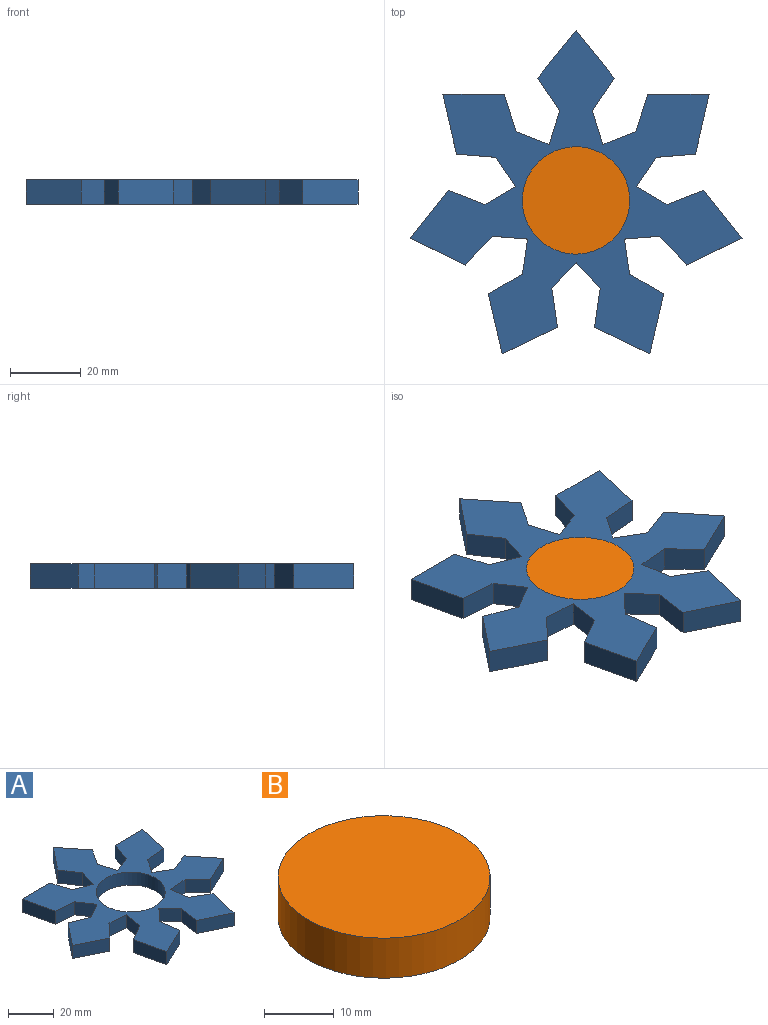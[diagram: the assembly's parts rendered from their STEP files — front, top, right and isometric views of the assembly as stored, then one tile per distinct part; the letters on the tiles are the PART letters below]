
ASSEMBLY  parts=2 mates=1
PART A: 45 faces, bbox 93.6x91.3x7 mm
  f0: plane 8.62x7mm, normal (0.5,0.86,0), area 69.9mm2, adj f1,f42,f43,f44
  f1: plane 8.27x7mm, normal (0.83,-0.56,0), area 69.9mm2, adj f0,f2,f43,f44
  f2: plane 11.07x7mm, normal (0.08,-1,0), area 77.7mm2, adj f1,f3,f43,f44
  f3: plane 16.89x7mm, normal (0.98,-0.22,0), area 121.2mm2, adj f2,f4,f43,f44
  f4: plane 17.32x7mm, normal (0,1,0), area 121.2mm2, adj f3,f5,f43,f44
  f5: plane 10.59x7mm, normal (-0.95,0.3,0), area 77.7mm2, adj f4,f6,f43,f44
  f6: plane 9.31x7mm, normal (-0.36,0.93,0), area 69.9mm2, adj f5,f7,f43,f44
  f7: plane 9.52x7mm, normal (0.95,0.3,0), area 69.9mm2, adj f6,f8,f43,f44
  f8: plane 9.21x7mm, normal (0.83,-0.56,0), area 77.7mm2, adj f7,f9,f43,f44
  f9: plane 13.53x10.81mm, normal (0.78,0.62,0), area 121.2mm2, adj f8,f10,f43,f44
  f10: plane 13.53x10.81mm, normal (-0.78,0.62,0), area 121.2mm2, adj f9,f11,f43,f44
  f11: plane 9.21x7mm, normal (-0.83,-0.56,0), area 77.7mm2, adj f10,f12,f43,f44
  f12: plane 9.52x7mm, normal (-0.95,0.3,0), area 69.9mm2, adj f11,f13,f43,f44
  f13: plane 9.31x7mm, normal (0.36,0.93,0), area 69.9mm2, adj f12,f14,f43,f44
  f14: plane 10.59x7mm, normal (0.95,0.3,0), area 77.7mm2, adj f13,f15,f43,f44
  f15: plane 17.32x7mm, normal (0,1,0), area 121.2mm2, adj f14,f16,f43,f44
  f16: plane 16.89x7mm, normal (-0.98,-0.22,0), area 121.2mm2, adj f15,f17,f43,f44
  f17: plane 11.07x7mm, normal (-0.08,-1,0), area 77.7mm2, adj f16,f18,f43,f44
  f18: plane 8.27x7mm, normal (-0.83,-0.56,0), area 69.9mm2, adj f17,f19,f43,f44
  f19: plane 8.62x7mm, normal (-0.5,0.86,0), area 69.9mm2, adj f18,f20,f43,f44
  f20: plane 10.36x7mm, normal (0.36,0.93,0), area 77.7mm2, adj f19,f21,f43,f44
  f21: plane 13.55x10.79mm, normal (-0.78,0.62,0), area 121.2mm2, adj f20,f22,f43,f44
  f22: plane 15.6x7.53mm, normal (-0.43,-0.9,0), area 121.2mm2, adj f21,f23,f43,f44
  f23: plane 8.1x7.6mm, normal (0.73,-0.68,0), area 77.7mm2, adj f22,f24,f43,f44
  f24: plane 9.95x7mm, normal (-0.08,-1,0), area 69.9mm2, adj f23,f25,f43,f44
  f25: plane 9.88x7mm, normal (-0.99,0.14,0), area 69.9mm2, adj f24,f26,f43,f44
  f26: plane 9.58x7mm, normal (-0.5,0.86,0), area 77.7mm2, adj f25,f27,f43,f44
  f27: plane 16.88x7mm, normal (-0.97,-0.22,0), area 121.2mm2, adj f26,f28,f43,f44
  f28: plane 15.61x7.5mm, normal (0.43,-0.9,0), area 121.2mm2, adj f27,f29,f43,f44
  f29: plane 10.99x7mm, normal (0.99,0.14,0), area 77.7mm2, adj f28,f30,f43,f44
  f30: plane 7.29x7mm, normal (0.73,-0.68,0), area 69.9mm2, adj f29,f31,f43,f44
  f31: plane 7.29x7mm, normal (-0.73,-0.68,0), area 69.9mm2, adj f30,f32,f43,f44
  f32: plane 10.99x7mm, normal (-0.99,0.14,0), area 77.7mm2, adj f31,f33,f43,f44
  f33: plane 15.61x7.5mm, normal (-0.43,-0.9,0), area 121.2mm2, adj f32,f34,f43,f44
  f34: plane 16.88x7mm, normal (0.97,-0.22,0), area 121.2mm2, adj f33,f35,f43,f44
  f35: plane 9.58x7mm, normal (0.5,0.86,0), area 77.7mm2, adj f34,f36,f43,f44
  f36: plane 9.88x7mm, normal (0.99,0.14,0), area 69.9mm2, adj f35,f37,f43,f44
  f37: plane 9.95x7mm, normal (0.08,-1,0), area 69.9mm2, adj f36,f38,f43,f44
  f38: plane 8.1x7.6mm, normal (-0.73,-0.68,0), area 77.7mm2, adj f37,f39,f43,f44
  f39: plane 15.6x7.53mm, normal (0.43,-0.9,0), area 121.2mm2, adj f38,f40,f43,f44
  f40: plane 13.55x10.79mm, normal (0.78,0.62,0), area 121.2mm2, adj f39,f42,f43,f44
  f41: cylinder r=15.16mm len=30.31mm, axis (0,0,-1), area 666.6mm2, adj f43,f44
  f42: plane 10.36x7mm, normal (-0.36,0.93,0), area 77.7mm2, adj f0,f40,f43,f44
  f43: plane 93.63x91.29mm, normal (0,0,1), area 2945.2mm2, adj f0,f1,f2,f3,f4,f5,f6,f7
  f44: plane 93.63x91.29mm, normal (0,0,-1), area 2945.2mm2, adj f0,f1,f2,f3,f4,f5,f6,f7
PART B: 3 faces, bbox 30.3x30.3x7 mm
  f0: cylinder r=15.16mm len=30.31mm, axis (0,0,-1), area 666.6mm2, adj f1,f2
  f1: plane 30.31x30.31mm, normal (0,0,1), area 721.6mm2, adj f0
  f2: plane 30.31x30.31mm, normal (0,0,-1), area 721.6mm2, adj f0
PLACE A t=(9.89,-15.57,11.17)mm
PLACE B t=(9.89,-15.57,11.17)mm
MATE revolute A.f41 <-> B.f0  axis (0,0,1) through (9.89,-15.57,18.17)mm
